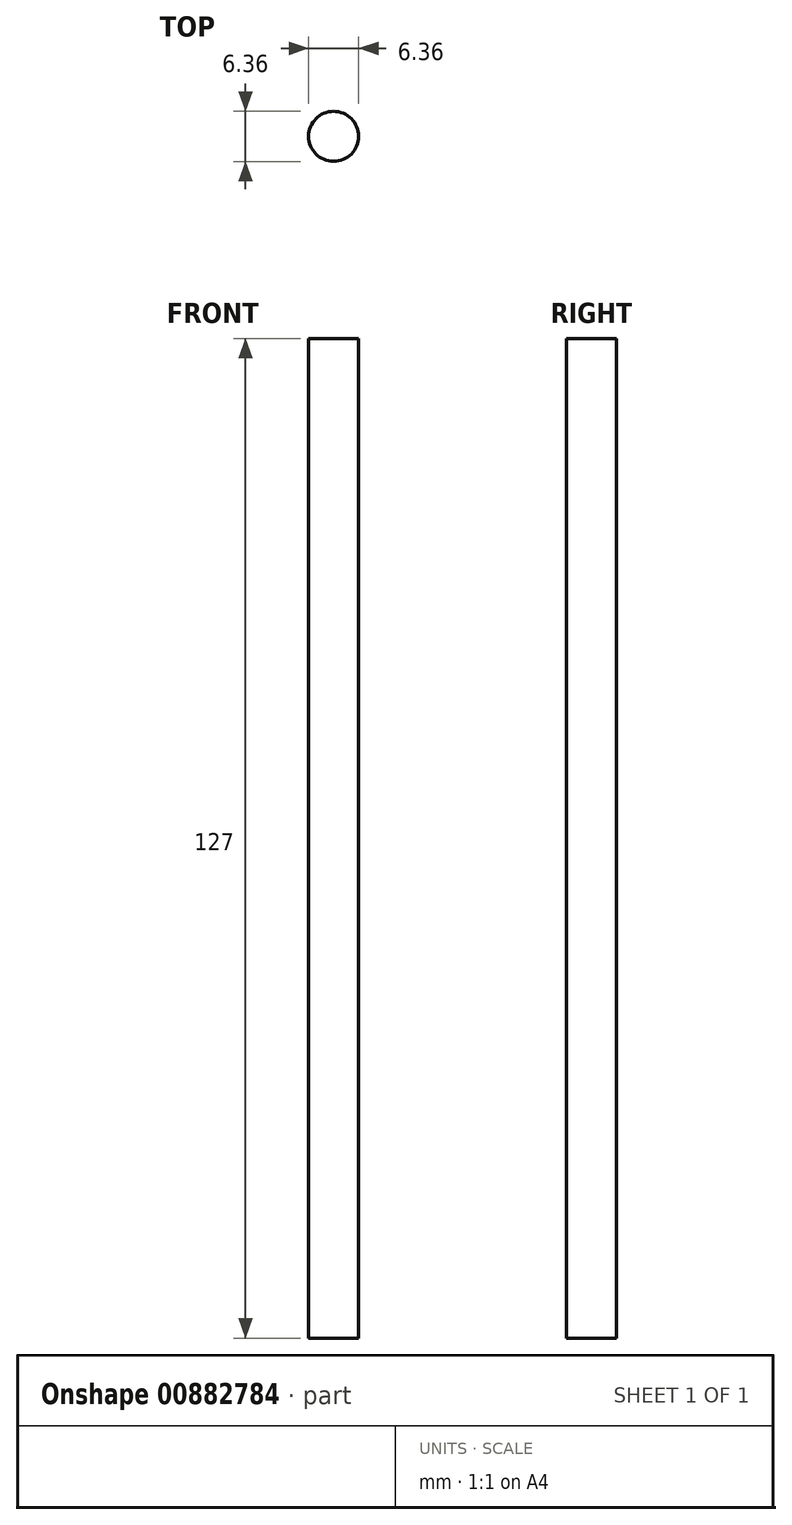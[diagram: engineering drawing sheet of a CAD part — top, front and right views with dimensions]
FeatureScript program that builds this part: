
annotation { "Feature Type Name" : "Feature", "Feature Type Description" : "" }
export const myFeature = defineFeature(function(context is Context, id is Id, definition is map)
    precondition{}
    {
        {
            var Q0;
            Q0=qCreatedBy(makeId("Top.planeOp"),FACE);
            var sketch = newSketch(context, id + "F0", { "sketchPlane" : qUnion([Q0])});
            skCircle(sketch, "E0", {"center": v(0, 0) * mm, "radius": 3.18 * mm});
            skSolve(sketch);
        }
        {
            var Q0;
            Q0=qSketchRegion(id+"F0",true);
            extrude(context, id + "F1", {"entities" : qUnion([Q0]), "depth" : 127 * mm, "offsetDistance" : 25.4 * mm});
        }
    });
